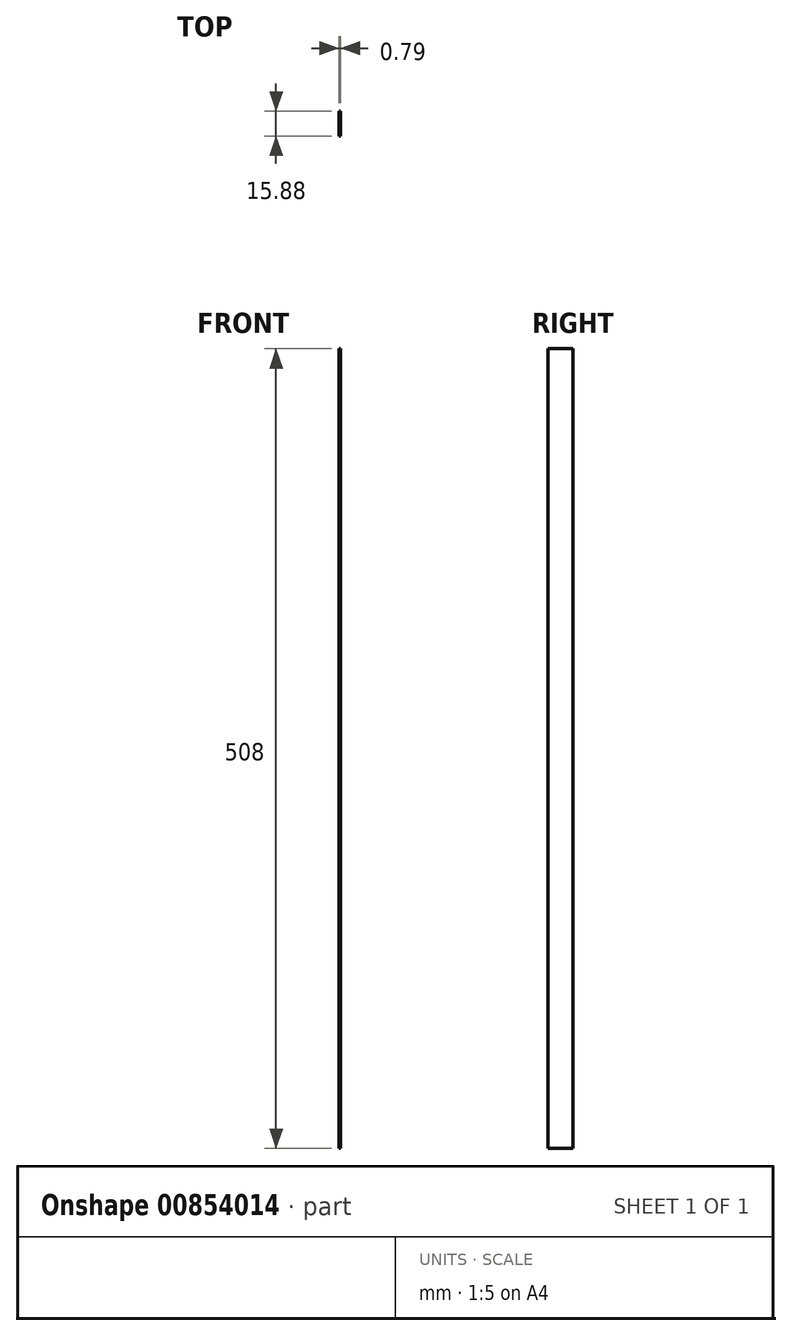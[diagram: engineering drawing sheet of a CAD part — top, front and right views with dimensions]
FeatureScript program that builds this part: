
annotation { "Feature Type Name" : "Feature", "Feature Type Description" : "" }
export const myFeature = defineFeature(function(context is Context, id is Id, definition is map)
    precondition{}
    {
        {
            var Q0;
            Q0=qCreatedBy(makeId("Front.planeOp"),FACE);
            var sketch = newSketch(context, id + "F0", { "sketchPlane" : qUnion([Q0])});
            skLineSegment(sketch, "E0.bottom", {"start": v(0, 508) * mm, "end": v(0.8, 508) * mm});
            skLineSegment(sketch, "E0.top", {"start": v(0, 0) * mm, "end": v(0.8, 0) * mm});
            skLineSegment(sketch, "E0.left", {"start": v(0, 508) * mm, "end": v(0, 0) * mm});
            skLineSegment(sketch, "E0.right", {"start": v(0.8, 508) * mm, "end": v(0.8, 0) * mm});
            skSolve(sketch);
        }
        {
            var Q0;
            Q0=makeQuery(id+"F0.imprint","IMPRINT",FACE,{"disambiguationData":[TD([[makeQuery(id+"F0.imprint","IMPRINT",EDGE,{"derivedFrom":sQuery(id+"F0.wireOp",EDGE,"E0.bottom")}),-1.0]])]});
            extrude(context, id + "F1", {"entities" : qUnion([Q0]), "oppositeDirection" : true, "depth" : 15.88 * mm, "offsetDistance" : 25.4 * mm});
        }
    });
